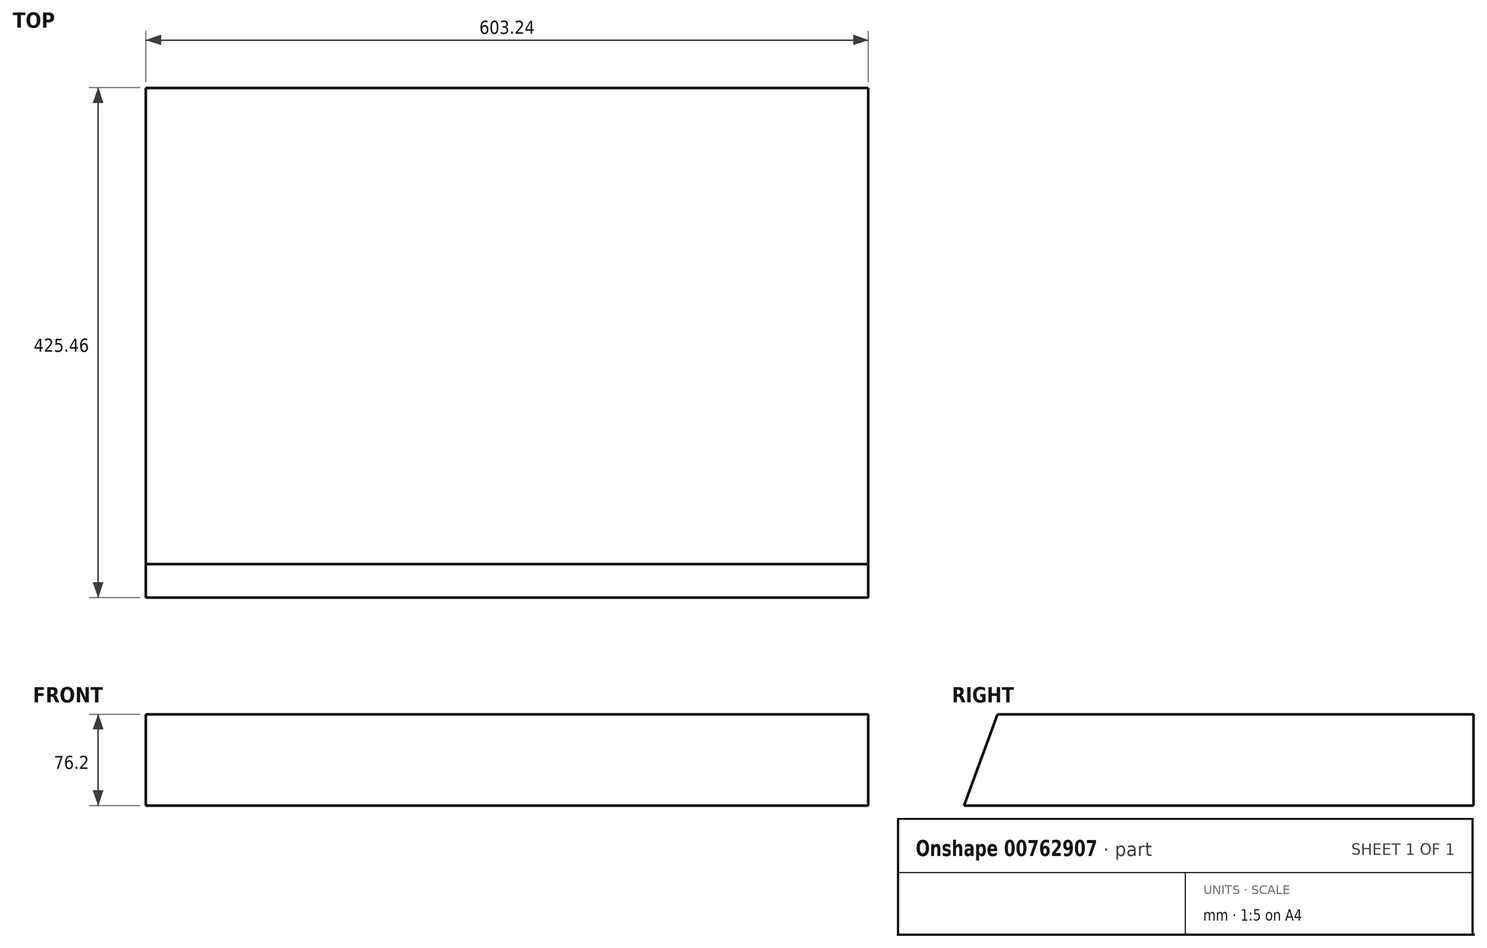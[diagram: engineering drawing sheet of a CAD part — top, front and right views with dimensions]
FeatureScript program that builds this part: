
annotation { "Feature Type Name" : "Feature", "Feature Type Description" : "" }
export const myFeature = defineFeature(function(context is Context, id is Id, definition is map)
    precondition{}
    {
        {
            var Q0;
            Q0=qCreatedBy(makeId("Right.planeOp"),FACE);
            var sketch = newSketch(context, id + "F0", { "sketchPlane" : qUnion([Q0])});
            skLineSegment(sketch, "E0", {"start": v(212.73, 0) * mm, "end": v(-212.73, 0) * mm});
            skLineSegment(sketch, "E1", {"start": v(212.73, 0) * mm, "end": v(212.73, 76.2) * mm});
            skLineSegment(sketch, "E2", {"start": v(212.73, 76.2) * mm, "end": v(-185, 76.2) * mm});
            skLineSegment(sketch, "E3", {"start": v(-185, 76.2) * mm, "end": v(-212.73, 0) * mm});
            skSolve(sketch);
        }
        {
            var Q0;
            Q0=makeQuery(id+"F0.imprint","IMPRINT",FACE,{"disambiguationData":[TD([[makeQuery(id+"F0.imprint","IMPRINT",EDGE,{"derivedFrom":sQuery(id+"F0.wireOp",EDGE,"E0")}),-1.0]])]});
            var Q1;
            Q1=sQuery(id+"F0.wireOp",EDGE,"E2");
            extrude(context, id + "F1", {"entities" : qUnion([Q0]), "surfaceEntities" : qUnion([Q1]), "depth" : 603.25 * mm, "offsetDistance" : 25.4 * mm, "symmetric" : true});
        }
    });
